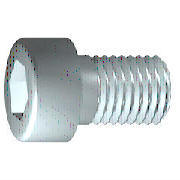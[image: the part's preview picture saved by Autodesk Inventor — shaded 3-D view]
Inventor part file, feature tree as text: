
AUTODESK INVENTOR PART (.ipt)
format: ipt  version: 2018 (Build 220112000, 112)  size: 189,440 bytes
history: native  units: mm (DEFAULTED — no unit token found)
features: sketch x2, extrude x1, plane x1, fillet x1
ambient origin geometry x7: Origin, YZ Plane, XY Plane, X Axis, Y Axis, Z Axis, Center Point
bodies: Solid1 (feature_tree), Body (feature_tree)
feature tree (5):
  extrude  "Slot"  Depth=3.0mm
  plane  "Work Plane1"
  fillet  "Fillet2"  Radius=3.0mm
  sketch  "Sketch1"  dims[d1=18.75mm d2=0.306825mm d3=3.0mm]
  sketch  "Sketch2"  dims[d4=1.3mm d5=60.0deg d6=3.0mm d7=3.0mm d8=2.886751mm d9=5.5mm d10=90.0deg d11=10.0mm d12=0.0mm d13=18.75mm d14=0.0mm d15=0.306725mm d16=0.306725mm d17=0.3mm d19=0.0mm d26=20.0mm d27=45.0deg d28=0.0mm d29=0.0mm d30=0.1mm]
